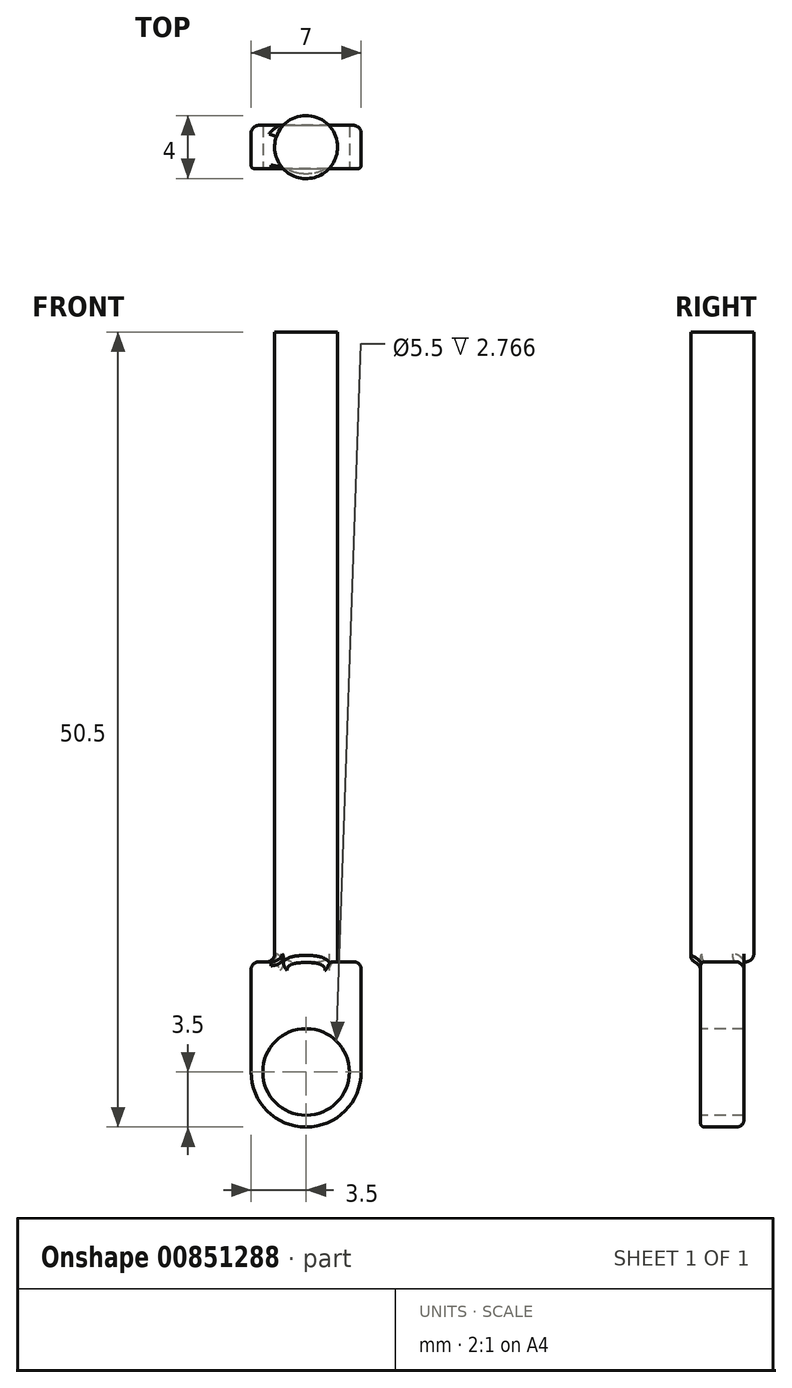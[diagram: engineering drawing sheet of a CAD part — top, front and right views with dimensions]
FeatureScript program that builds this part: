
annotation { "Feature Type Name" : "Feature", "Feature Type Description" : "" }
export const myFeature = defineFeature(function(context is Context, id is Id, definition is map)
    precondition{}
    {
        {
            var Q0;
            Q0=qCreatedBy(makeId("Front.planeOp"),FACE);
            var sketch = newSketch(context, id + "F0", { "sketchPlane" : qUnion([Q0])});
            skCircle(sketch, "E0", {"center": v(0, 0) * mm, "radius": 3.5 * mm});
            skLineSegment(sketch, "E1.bottom", {"start": v(-3.5, 0) * mm, "end": v(3.5, 0) * mm});
            skLineSegment(sketch, "E1.top", {"start": v(-3.5, 7) * mm, "end": v(3.5, 7) * mm});
            skLineSegment(sketch, "E1.left", {"start": v(-3.5, 0) * mm, "end": v(-3.5, 7) * mm});
            skLineSegment(sketch, "E1.right", {"start": v(3.5, 0) * mm, "end": v(3.5, 7) * mm});
            skSolve(sketch);
        }
        {
            var Q0;
            Q0=makeQuery(id+"F0.imprint","IMPRINT",FACE,{"disambiguationData":[TD([[makeQuery(id+"F0.imprint","IMPRINT",EDGE,{"derivedFrom":sQuery(id+"F0.wireOp",EDGE,"E1.top")}),-1.0]])]});
            var Q1;
            {var subQ0=sQuery(id+"F0.wireOp",EDGE,"E1.bottom");Q1=makeQuery(id+"F0.imprint","IMPRINT",FACE,{"disambiguationData":[TD([[makeQuery(id+"F0.imprint","IMPRINT",EDGE,{"derivedFrom":subQ0}),1.0]])]});}
            var Q2;
            {var subQ0=sQuery(id+"F0.wireOp",EDGE,"E1.bottom");Q2=makeQuery(id+"F0.imprint","IMPRINT",FACE,{"disambiguationData":[TD([[makeQuery(id+"F0.imprint","IMPRINT",EDGE,{"derivedFrom":subQ0}),-1.0]])]});}
            extrude(context, id + "F1", {"entities" : qUnion([Q0, Q1, Q2]), "depth" : 2.77 * mm, "offsetDistance" : 25 * mm});
        }
        {
            var Q0;
            Q0=makeQuery(id+"F1.opExtrude","CAP_FACE",FACE,{"disambiguationData":[OSD([sQuery(id+"F0.wireOp",EDGE,"E0"),sQuery(id+"F0.wireOp",EDGE,"E1.top"),sQuery(id+"F0.wireOp",EDGE,"E1.left"),sQuery(id+"F0.wireOp",EDGE,"E1.right")])],"isStart":false});
            var sketch = newSketch(context, id + "F2", { "sketchPlane" : qUnion([Q0])});
            skCircle(sketch, "E2", {"center": v(0, 0) * mm, "radius": 2.75 * mm});
            skSolve(sketch);
        }
        {
            var Q0;
            Q0=makeQuery(id+"F2.imprint","IMPRINT",FACE,{"disambiguationData":[TD([[makeQuery(id+"F2.imprint","IMPRINT",EDGE,{"derivedFrom":sQuery(id+"F2.wireOp",EDGE,"E2")}),1.0]])]});
            extrude(context, id + "F3", {"entities" : qUnion([Q0]), "operationType" : NewBodyOperationType.REMOVE, "oppositeDirection" : true, "depth" : 25 * mm, "offsetDistance" : 25 * mm});
        }
        {
            var Q0;
            Q0=makeQuery(id+"F1.opExtrude","SWEPT_FACE",FACE,{"disambiguationData":[OSD([sQuery(id+"F0.wireOp",EDGE,"E1.top")])]});
            var sketch = newSketch(context, id + "F4", { "sketchPlane" : qUnion([Q0])});
            skLineSegment(sketch, "E3", {"start": v(0, 0) * mm, "end": v(0, -2.77) * mm});
            skCircle(sketch, "E4", {"center": v(0, -1.38) * mm, "radius": 2 * mm});
            skSolve(sketch);
        }
        {
            var Q0;
            {var subQ0=sQuery(id+"F4.wireOp",EDGE,"E3");Q0=makeQuery(id+"F4.imprint","IMPRINT",FACE,{"disambiguationData":[TD([[makeQuery(id+"F4.imprint","IMPRINT",EDGE,{"derivedFrom":subQ0}),1.0]])]});}
            var Q1;
            {var subQ0=sQuery(id+"F4.wireOp",EDGE,"E4");var subQ1=makeQuery(id+"F1.opExtrude","CAP_EDGE",EDGE,{"disambiguationData":[OSD([sQuery(id+"F0.wireOp",EDGE,"E1.top")])],"isStart":true});var subQ2=makeQuery(id+"F4.imprint","INTERSECT",VERTEX,{"disambiguationData":[OD(0.0)],"derivedFrom":[subQ1,subQ0]});Q1=makeQuery(id+"F4.imprint","IMPRINT",FACE,{"disambiguationData":[TD([[makeQuery(id+"F4.imprint","IMPRINT",EDGE,{"disambiguationData":[TD([[subQ2,1.0]])],"derivedFrom":subQ0}),1.0]])]});}
            var Q2;
            {var subQ0=sQuery(id+"F4.wireOp",EDGE,"E4");var subQ1=makeQuery(id+"F1.opExtrude","CAP_EDGE",EDGE,{"disambiguationData":[OSD([sQuery(id+"F0.wireOp",EDGE,"E1.top")])],"isStart":false});var subQ2=makeQuery(id+"F4.imprint","INTERSECT",VERTEX,{"disambiguationData":[OD(0.0)],"derivedFrom":[subQ1,subQ0]});Q2=makeQuery(id+"F4.imprint","IMPRINT",FACE,{"disambiguationData":[TD([[makeQuery(id+"F4.imprint","IMPRINT",EDGE,{"disambiguationData":[TD([[subQ2,-1.0]])],"derivedFrom":subQ0}),1.0]])]});}
            var Q3;
            {var subQ0=sQuery(id+"F4.wireOp",EDGE,"E3");Q3=makeQuery(id+"F4.imprint","IMPRINT",FACE,{"disambiguationData":[TD([[makeQuery(id+"F4.imprint","IMPRINT",EDGE,{"derivedFrom":subQ0}),-1.0]])]});}
            extrude(context, id + "F5", {"entities" : qUnion([Q0, Q1, Q2, Q3]), "operationType" : NewBodyOperationType.ADD, "depth" : 40 * mm, "offsetDistance" : 25 * mm});
        }
        {
            var Q0;
            {var subQ0=sQuery(id+"F0.wireOp",EDGE,"E1.top");Q0=makeQuery(id+"F5.boolean.opBoolean","SPLIT",EDGE,{"disambiguationData":[topologyDisambiguationEdgeConnected([makeQuery(id+"F1.opExtrude","CAP_FACE",FACE,{"disambiguationData":[OSD([sQuery(id+"F0.wireOp",EDGE,"E0"),subQ0,sQuery(id+"F0.wireOp",EDGE,"E1.left"),sQuery(id+"F0.wireOp",EDGE,"E1.right")])],"isStart":false}),makeQuery(id+"F5.opExtrude","CAP_FACE",FACE,{"disambiguationData":[OSD([sQuery(id+"F4.wireOp",EDGE,"E4")])],"isStart":true})])],"derivedFrom":makeQuery(id+"F1.opExtrude","CAP_EDGE",EDGE,{"disambiguationData":[OSD([subQ0])],"isStart":false})});}
            var Q1;
            {var subQ0=sQuery(id+"F0.wireOp",EDGE,"E1.top");Q1=makeQuery(id+"F5.boolean.opBoolean","SPLIT",EDGE,{"disambiguationData":[topologyDisambiguationEdgeConnected([makeQuery(id+"F1.opExtrude","CAP_FACE",FACE,{"disambiguationData":[OSD([sQuery(id+"F0.wireOp",EDGE,"E0"),subQ0,sQuery(id+"F0.wireOp",EDGE,"E1.left"),sQuery(id+"F0.wireOp",EDGE,"E1.right")])],"isStart":true}),makeQuery(id+"F5.opExtrude","CAP_FACE",FACE,{"disambiguationData":[OSD([sQuery(id+"F4.wireOp",EDGE,"E4")])],"isStart":true})])],"derivedFrom":makeQuery(id+"F1.opExtrude","CAP_EDGE",EDGE,{"disambiguationData":[OSD([subQ0])],"isStart":true})});}
            fillet(context, id + "F6", {"entities" : qUnion([Q0, Q1]), "radius" : 0.55 * mm, "tangentPropagation" : true, "allowEdgeOverflow" : false});
        }
        {
            var Q0;
            Q0=makeQuery(id+"F1.opExtrude","SWEPT_EDGE",EDGE,{"disambiguationData":[OSD([sQuery(id+"F0.wireOp",EDGE,"E1.top"),sQuery(id+"F0.wireOp",EDGE,"E1.left")])]});
            var Q1;
            {var subQ0=sQuery(id+"F4.wireOp",EDGE,"E4");Q1=makeQuery(id+"F5.boolean.opBoolean","SPLIT",EDGE,{"disambiguationData":[topologyDisambiguationEdgeConnected([makeQuery(id+"F1.opExtrude","SWEPT_FACE",FACE,{"disambiguationData":[OSD([sQuery(id+"F0.wireOp",EDGE,"E1.top")])]}),makeQuery(id+"F5.opExtrude","SWEPT_FACE",FACE,{"disambiguationData":[OSD([subQ0])]})]),OD(0.0)],"derivedFrom":makeQuery(id+"F5.opExtrude","CAP_EDGE",EDGE,{"disambiguationData":[OSD([subQ0])],"isStart":true})});}
            var Q2;
            {var subQ0=sQuery(id+"F0.wireOp",EDGE,"E1.top");var subQ1=sQuery(id+"F4.wireOp",EDGE,"E4");var subQ2=makeQuery(id+"F5.opExtrude","CAP_FACE",FACE,{"disambiguationData":[OSD([subQ1])],"isStart":true});var subQ3=makeQuery(id+"F5.opExtrude","SWEPT_FACE",FACE,{"disambiguationData":[OSD([subQ1])]});Q2=makeQuery(id+"F5.boolean.opBoolean","SPLIT",EDGE,{"disambiguationData":[topologyDisambiguationEdgeConnected([subQ3,subQ2]),TD([makeQuery(id+"F1.opExtrude","CAP_FACE",FACE,{"disambiguationData":[OSD([sQuery(id+"F0.wireOp",EDGE,"E0"),subQ0,sQuery(id+"F0.wireOp",EDGE,"E1.left"),sQuery(id+"F0.wireOp",EDGE,"E1.right")])],"isStart":true})])],"derivedFrom":makeQuery(id+"F5.opExtrude","CAP_EDGE",EDGE,{"disambiguationData":[OSD([subQ1])],"isStart":true})});}
            var Q3;
            {var subQ0=sQuery(id+"F4.wireOp",EDGE,"E4");Q3=makeQuery(id+"F5.boolean.opBoolean","SPLIT",EDGE,{"disambiguationData":[topologyDisambiguationEdgeConnected([makeQuery(id+"F1.opExtrude","SWEPT_FACE",FACE,{"disambiguationData":[OSD([sQuery(id+"F0.wireOp",EDGE,"E1.top")])]}),makeQuery(id+"F5.opExtrude","SWEPT_FACE",FACE,{"disambiguationData":[OSD([subQ0])]})]),OD(1.0)],"derivedFrom":makeQuery(id+"F5.opExtrude","CAP_EDGE",EDGE,{"disambiguationData":[OSD([subQ0])],"isStart":true})});}
            var Q4;
            Q4=makeQuery(id+"F1.opExtrude","SWEPT_EDGE",EDGE,{"disambiguationData":[OSD([sQuery(id+"F0.wireOp",EDGE,"E1.top"),sQuery(id+"F0.wireOp",EDGE,"E1.right")])]});
            var Q5;
            {var subQ0=sQuery(id+"F0.wireOp",EDGE,"E1.top");var subQ1=sQuery(id+"F4.wireOp",EDGE,"E4");var subQ2=makeQuery(id+"F5.opExtrude","SWEPT_FACE",FACE,{"disambiguationData":[OSD([subQ1])]});var subQ3=makeQuery(id+"F5.opExtrude","CAP_FACE",FACE,{"disambiguationData":[OSD([subQ1])],"isStart":true});Q5=makeQuery(id+"F5.boolean.opBoolean","SPLIT",EDGE,{"disambiguationData":[topologyDisambiguationEdgeConnected([subQ2,subQ3]),TD([makeQuery(id+"F1.opExtrude","CAP_FACE",FACE,{"disambiguationData":[OSD([sQuery(id+"F0.wireOp",EDGE,"E0"),subQ0,sQuery(id+"F0.wireOp",EDGE,"E1.left"),sQuery(id+"F0.wireOp",EDGE,"E1.right")])],"isStart":false})])],"derivedFrom":makeQuery(id+"F5.opExtrude","CAP_EDGE",EDGE,{"disambiguationData":[OSD([subQ1])],"isStart":true})});}
            fillet(context, id + "F7", {"entities" : qUnion([Q0, Q1, Q2, Q3, Q4, Q5]), "radius" : 0.5 * mm, "tangentPropagation" : true, "allowEdgeOverflow" : false});
        }
        {
            var Q0;
            {var subQ1=sQuery(id+"F0.wireOp",EDGE,"E1.right");var subQ2=sQuery(id+"F0.wireOp",EDGE,"E1.top");var subQ3=makeQuery(id+"F1.opExtrude","SWEPT_FACE",FACE,{"disambiguationData":[OSD([subQ2])]});var subQ4=makeQuery(id+"F1.opExtrude","CAP_FACE",FACE,{"disambiguationData":[OSD([sQuery(id+"F0.wireOp",EDGE,"E0"),subQ2,sQuery(id+"F0.wireOp",EDGE,"E1.left"),subQ1])],"isStart":true});Q0=makeQuery(id+"F5.boolean.opBoolean","SPLIT",EDGE,{"disambiguationData":[topologyDisambiguationEdgeConnected([subQ4,subQ3]),TD([makeQuery(id+"F1.opExtrude","SWEPT_FACE",FACE,{"disambiguationData":[OSD([subQ1])]})])],"derivedFrom":makeQuery(id+"F1.opExtrude","CAP_EDGE",EDGE,{"disambiguationData":[OSD([subQ2])],"isStart":true})});}
            var Q1;
            {var subQ1=sQuery(id+"F0.wireOp",EDGE,"E1.left");var subQ2=sQuery(id+"F0.wireOp",EDGE,"E1.top");var subQ3=makeQuery(id+"F1.opExtrude","SWEPT_FACE",FACE,{"disambiguationData":[OSD([subQ2])]});var subQ4=makeQuery(id+"F1.opExtrude","CAP_FACE",FACE,{"disambiguationData":[OSD([sQuery(id+"F0.wireOp",EDGE,"E0"),subQ2,subQ1,sQuery(id+"F0.wireOp",EDGE,"E1.right")])],"isStart":true});Q1=makeQuery(id+"F5.boolean.opBoolean","SPLIT",EDGE,{"disambiguationData":[topologyDisambiguationEdgeConnected([subQ4,subQ3]),TD([makeQuery(id+"F1.opExtrude","SWEPT_FACE",FACE,{"disambiguationData":[OSD([subQ1])]})])],"derivedFrom":makeQuery(id+"F1.opExtrude","CAP_EDGE",EDGE,{"disambiguationData":[OSD([subQ2])],"isStart":true})});}
            var Q2;
            {var subQ0=sQuery(id+"F0.wireOp",EDGE,"E1.left");var subQ1=sQuery(id+"F0.wireOp",EDGE,"E1.top");var subQ2=makeQuery(id+"F1.opExtrude","SWEPT_FACE",FACE,{"disambiguationData":[OSD([subQ1])]});var subQ4=makeQuery(id+"F1.opExtrude","CAP_FACE",FACE,{"disambiguationData":[OSD([sQuery(id+"F0.wireOp",EDGE,"E0"),subQ1,subQ0,sQuery(id+"F0.wireOp",EDGE,"E1.right")])],"isStart":false});Q2=makeQuery(id+"F5.boolean.opBoolean","SPLIT",EDGE,{"disambiguationData":[topologyDisambiguationEdgeConnected([subQ4,subQ2]),TD([makeQuery(id+"F1.opExtrude","SWEPT_FACE",FACE,{"disambiguationData":[OSD([subQ0])]})])],"derivedFrom":makeQuery(id+"F1.opExtrude","CAP_EDGE",EDGE,{"disambiguationData":[OSD([subQ1])],"isStart":false})});}
            var Q3;
            {var subQ0=sQuery(id+"F0.wireOp",EDGE,"E1.right");var subQ1=sQuery(id+"F0.wireOp",EDGE,"E1.top");var subQ2=makeQuery(id+"F1.opExtrude","SWEPT_FACE",FACE,{"disambiguationData":[OSD([subQ1])]});var subQ4=makeQuery(id+"F1.opExtrude","CAP_FACE",FACE,{"disambiguationData":[OSD([sQuery(id+"F0.wireOp",EDGE,"E0"),subQ1,sQuery(id+"F0.wireOp",EDGE,"E1.left"),subQ0])],"isStart":false});Q3=makeQuery(id+"F5.boolean.opBoolean","SPLIT",EDGE,{"disambiguationData":[topologyDisambiguationEdgeConnected([subQ4,subQ2]),TD([makeQuery(id+"F1.opExtrude","SWEPT_FACE",FACE,{"disambiguationData":[OSD([subQ0])]})])],"derivedFrom":makeQuery(id+"F1.opExtrude","CAP_EDGE",EDGE,{"disambiguationData":[OSD([subQ1])],"isStart":false})});}
            fillet(context, id + "F8", {"entities" : qUnion([Q0, Q1, Q2, Q3]), "radius" : 0.25 * mm, "tangentPropagation" : true, "allowEdgeOverflow" : false});
        }
    });
